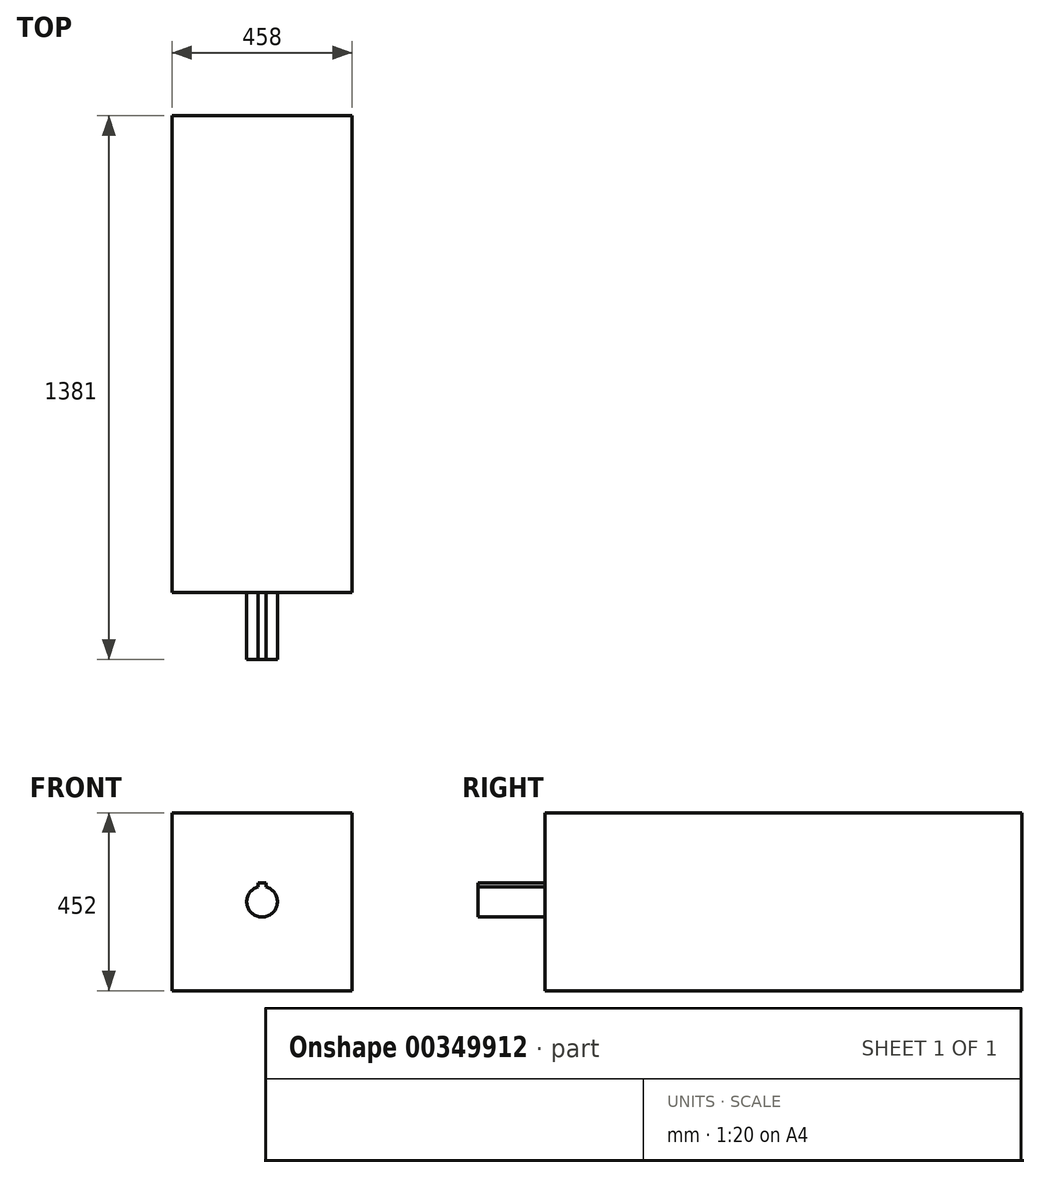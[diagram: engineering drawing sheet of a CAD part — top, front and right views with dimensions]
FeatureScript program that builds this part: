
annotation { "Feature Type Name" : "Feature", "Feature Type Description" : "" }
export const myFeature = defineFeature(function(context is Context, id is Id, definition is map)
    precondition{}
    {
        {
            var Q0;
            Q0=qCreatedBy(makeId("Front.planeOp"),FACE);
            var sketch = newSketch(context, id + "F0", { "sketchPlane" : qUnion([Q0])});
            skLineSegment(sketch, "E0.bottom", {"start": v(229, -226) * mm, "end": v(-229, -226) * mm});
            skLineSegment(sketch, "E0.top", {"start": v(229, 226) * mm, "end": v(-229, 226) * mm});
            skLineSegment(sketch, "E0.left", {"start": v(229, -226) * mm, "end": v(229, 226) * mm});
            skLineSegment(sketch, "E0.right", {"start": v(-229, -226) * mm, "end": v(-229, 226) * mm});
            skPoint(sketch, "E0.middle", {"position": v(0, 0) * mm});
            skSolve(sketch);
        }
        {
            var Q0;
            Q0 = qSketchRegion(id + "F0", true);
            extrude(context, id + "F1", {"entities" : qUnion([Q0]), "depth" : 1211 * mm, "offsetDistance" : 25.4 * mm});
        }
        {
            var Q0;
            Q0=makeQuery(id+"F1.opExtrude","CAP_FACE",FACE,{"disambiguationData":[OSD([sQuery(id+"F0.wireOp",EDGE,"E0.bottom"),sQuery(id+"F0.wireOp",EDGE,"E0.top"),sQuery(id+"F0.wireOp",EDGE,"E0.left"),sQuery(id+"F0.wireOp",EDGE,"E0.right")])],"isStart":false});
            var sketch = newSketch(context, id + "F2", { "sketchPlane" : qUnion([Q0])});
            skCircle(sketch, "E1", {"center": v(0, 0) * mm, "radius": 39.01 * mm});
            skLineSegment(sketch, "E2.bottom", {"start": v(10.26, 30.78) * mm, "end": v(-10.26, 30.78) * mm});
            skLineSegment(sketch, "E2.top", {"start": v(10.26, 47.25) * mm, "end": v(-10.26, 47.25) * mm});
            skLineSegment(sketch, "E2.left", {"start": v(10.26, 30.78) * mm, "end": v(10.26, 47.25) * mm});
            skLineSegment(sketch, "E2.right", {"start": v(-10.26, 30.78) * mm, "end": v(-10.26, 47.25) * mm});
            skPoint(sketch, "E2.middle", {"position": v(0, 39.01) * mm});
            skSolve(sketch);
        }
        {
            var Q0;
            Q0 = qSketchRegion(id + "F2", true);
            extrude(context, id + "F3", {"entities" : qUnion([Q0]), "operationType" : NewBodyOperationType.ADD, "depth" : 170 * mm, "offsetDistance" : 25.4 * mm});
        }
    });
